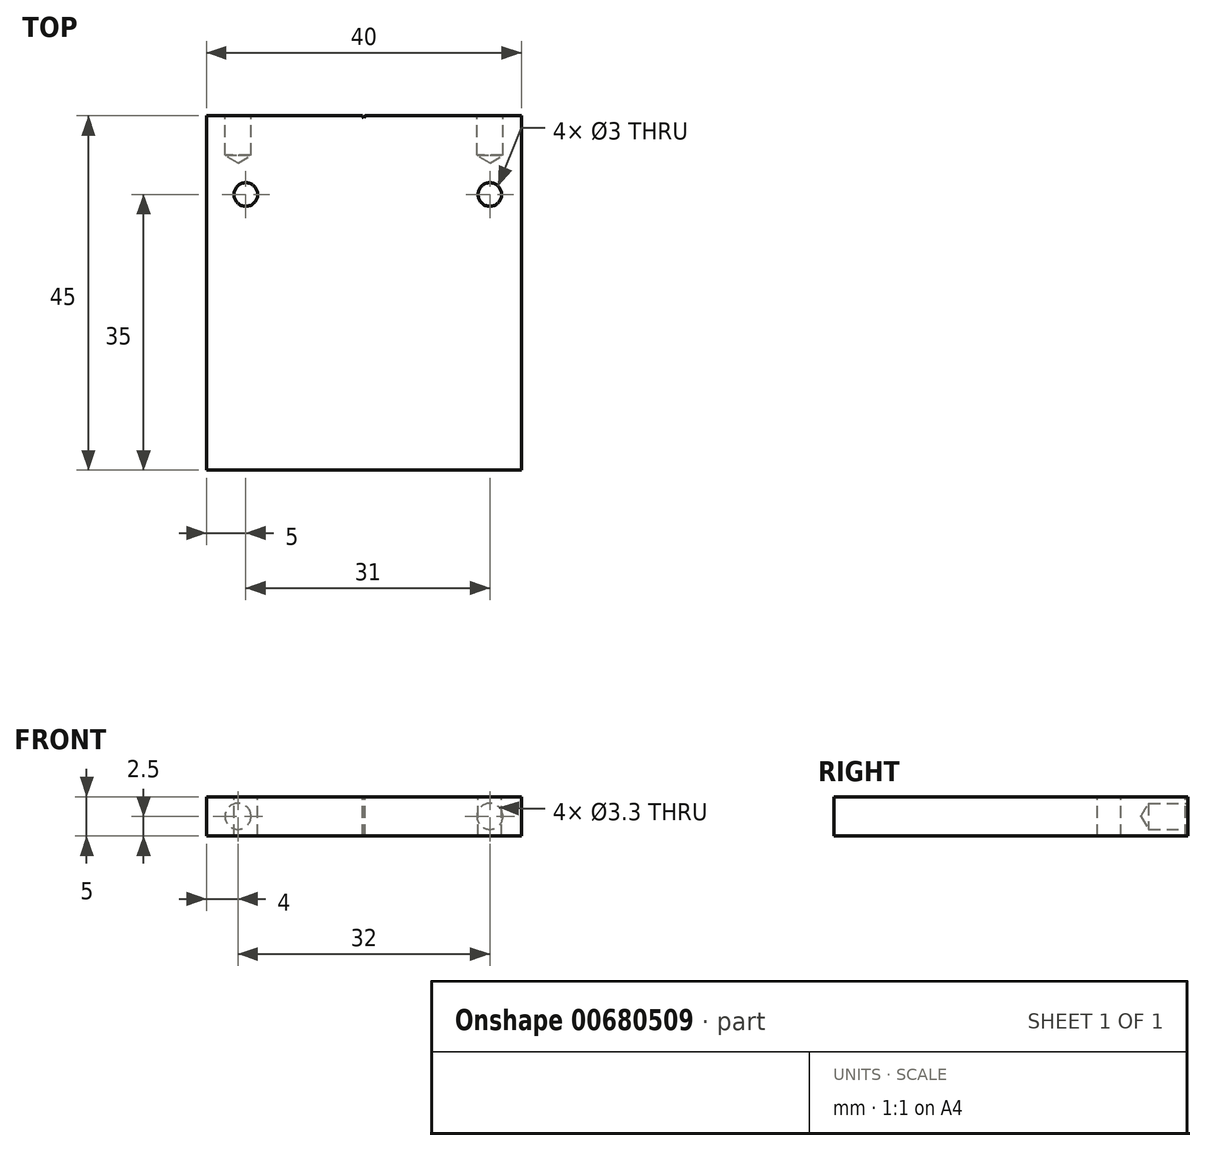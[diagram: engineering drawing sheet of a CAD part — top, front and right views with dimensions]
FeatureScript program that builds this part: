
annotation { "Feature Type Name" : "Feature", "Feature Type Description" : "" }
export const myFeature = defineFeature(function(context is Context, id is Id, definition is map)
    precondition{}
    {
        {
            var Q0;
            Q0=qCreatedBy(makeId("Top.planeOp"),FACE);
            var sketch = newSketch(context, id + "F0", { "sketchPlane" : qUnion([Q0])});
            skLineSegment(sketch, "E0.bottom", {"start": v(-20, 22.5) * mm, "end": v(20, 22.5) * mm});
            skLineSegment(sketch, "E0.top", {"start": v(-20, -22.5) * mm, "end": v(20, -22.5) * mm});
            skLineSegment(sketch, "E0.left", {"start": v(-20, 22.5) * mm, "end": v(-20, -22.5) * mm});
            skLineSegment(sketch, "E0.right", {"start": v(20, 22.5) * mm, "end": v(20, -22.5) * mm});
            skPoint(sketch, "E0.middle", {"position": v(0, 0) * mm});
            skSolve(sketch);
        }
        {
            var Q0;
            Q0=qSketchRegion(id+"F0",true);
            extrude(context, id + "F1", {"entities" : qUnion([Q0]), "depth" : 5 * mm, "offsetDistance" : 25 * mm});
        }
        {
            var Q0;
            Q0=makeQuery(id+"F1.opExtrude","CAP_FACE",FACE,{"disambiguationData":[OSD([sQuery(id+"F0.wireOp",EDGE,"E0.bottom"),sQuery(id+"F0.wireOp",EDGE,"E0.top"),sQuery(id+"F0.wireOp",EDGE,"E0.left"),sQuery(id+"F0.wireOp",EDGE,"E0.right")])],"isStart":false});
            var sketch = newSketch(context, id + "F2", { "sketchPlane" : qUnion([Q0])});
            skCircle(sketch, "E1", {"center": v(16, 12.5) * mm, "radius": 1.5 * mm});
            skCircle(sketch, "E2", {"center": v(-15, 12.5) * mm, "radius": 1.5 * mm});
            skSolve(sketch);
        }
        {
            var Q0;
            Q0=qSketchRegion(id+"F2",true);
            extrude(context, id + "F3", {"entities" : qUnion([Q0]), "operationType" : NewBodyOperationType.REMOVE, "oppositeDirection" : true, "depth" : 25 * mm, "offsetDistance" : 25 * mm});
        }
        {
            var Q0;
            Q0=makeQuery(id+"F2.imprint","IMPRINT",FACE,{"disambiguationData":[TD([[makeQuery(id+"F2.imprint","IMPRINT",EDGE,{"derivedFrom":sQuery(id+"F2.wireOp",EDGE,"E1")}),-1.0]])]});
            var sketch = newSketch(context, id + "F4", { "sketchPlane" : qUnion([Q0])});
            skCircle(sketch, "E3.cCircle", {"center": v(0, 22.4) * mm, "radius": 0.1 * mm, "construction": true});
            skLineSegment(sketch, "E3.0", {"start": v(-0.17, 22.5) * mm, "end": v(0.17, 22.5) * mm});
            skLineSegment(sketch, "E3.1", {"start": v(0.17, 22.5) * mm, "end": v(0, 22.2) * mm});
            skLineSegment(sketch, "E3.2", {"start": v(0, 22.2) * mm, "end": v(-0.17, 22.5) * mm});
            skPoint(sketch, "E3.0.midPoint", {"position": v(0, 22.5) * mm});
            skSolve(sketch);
        }
        {
            var Q0;
            Q0=qSketchRegion(id+"F4",true);
            extrude(context, id + "F5", {"entities" : qUnion([Q0]), "operationType" : NewBodyOperationType.REMOVE, "oppositeDirection" : true, "depth" : 25 * mm, "offsetDistance" : 25 * mm});
        }
        {
            var Q0;
            {var subQ0=sQuery(id+"F0.wireOp",EDGE,"E0.right");var subQ3=sQuery(id+"F0.wireOp",EDGE,"E0.bottom");Q0=makeQuery(id+"F5.boolean.opBoolean","SPLIT",FACE,{"disambiguationData":[TD([makeQuery(id+"F1.opExtrude","SWEPT_FACE",FACE,{"disambiguationData":[OSD([subQ0])]})])],"derivedFrom":makeQuery(id+"F1.opExtrude","SWEPT_FACE",FACE,{"disambiguationData":[OSD([subQ3])]})});}
            var sketch = newSketch(context, id + "F6", { "sketchPlane" : qUnion([Q0])});
            skPoint(sketch, "E4", {"position": v(-16, 2.5) * mm});
            skPoint(sketch, "E4.positionSnap0", {"position": v(-20, 2.5) * mm});
            skPoint(sketch, "E5", {"position": v(16, 2.5) * mm});
            skPoint(sketch, "E5.positionSnap0", {"position": v(-0.17, 2.5) * mm});
            skSolve(sketch);
        }
        {
            var Q0;
            Q0=sQuery(id+"F6.wireOp",VERTEX,"E4");
            var Q1;
            Q1=sQuery(id+"F6.wireOp",VERTEX,"E5");
            var Q2;
            Q2=makeQuery(id+"F1.opExtrude","SWEPT_BODY",BODY,{"disambiguationData":[OSD([sQuery(id+"F0.wireOp",EDGE,"E0.bottom"),sQuery(id+"F0.wireOp",EDGE,"E0.top"),sQuery(id+"F0.wireOp",EDGE,"E0.left"),sQuery(id+"F0.wireOp",EDGE,"E0.right")])]});
            hole(context, id + "F7", {"style" : HoleStyle.SIMPLE, "endStyle" : HoleEndStyle.BLIND, "standardTappedOrClearance" : lookupTablePath({ "standard" : "ISO", "fit" : "Normal", "size" : "M3", "type" : "Clearance" }), "standardBlindInLast" : lookupTablePath({ "fit" : "Standard", "standard" : "ISO", "size" : "M3", "type" : "Clearance" }), "holeDiameter" : 3.3 * mm, "majorDiameter" : 5 * mm, "holeDepth" : 5 * mm, "isTappedThrough" : true, "tappedDepth" : 12 * mm, "tapClearance" : 3, "locations" : qUnion([Q0, Q1]), "scope" : qUnion([Q2])});
        }
    });
